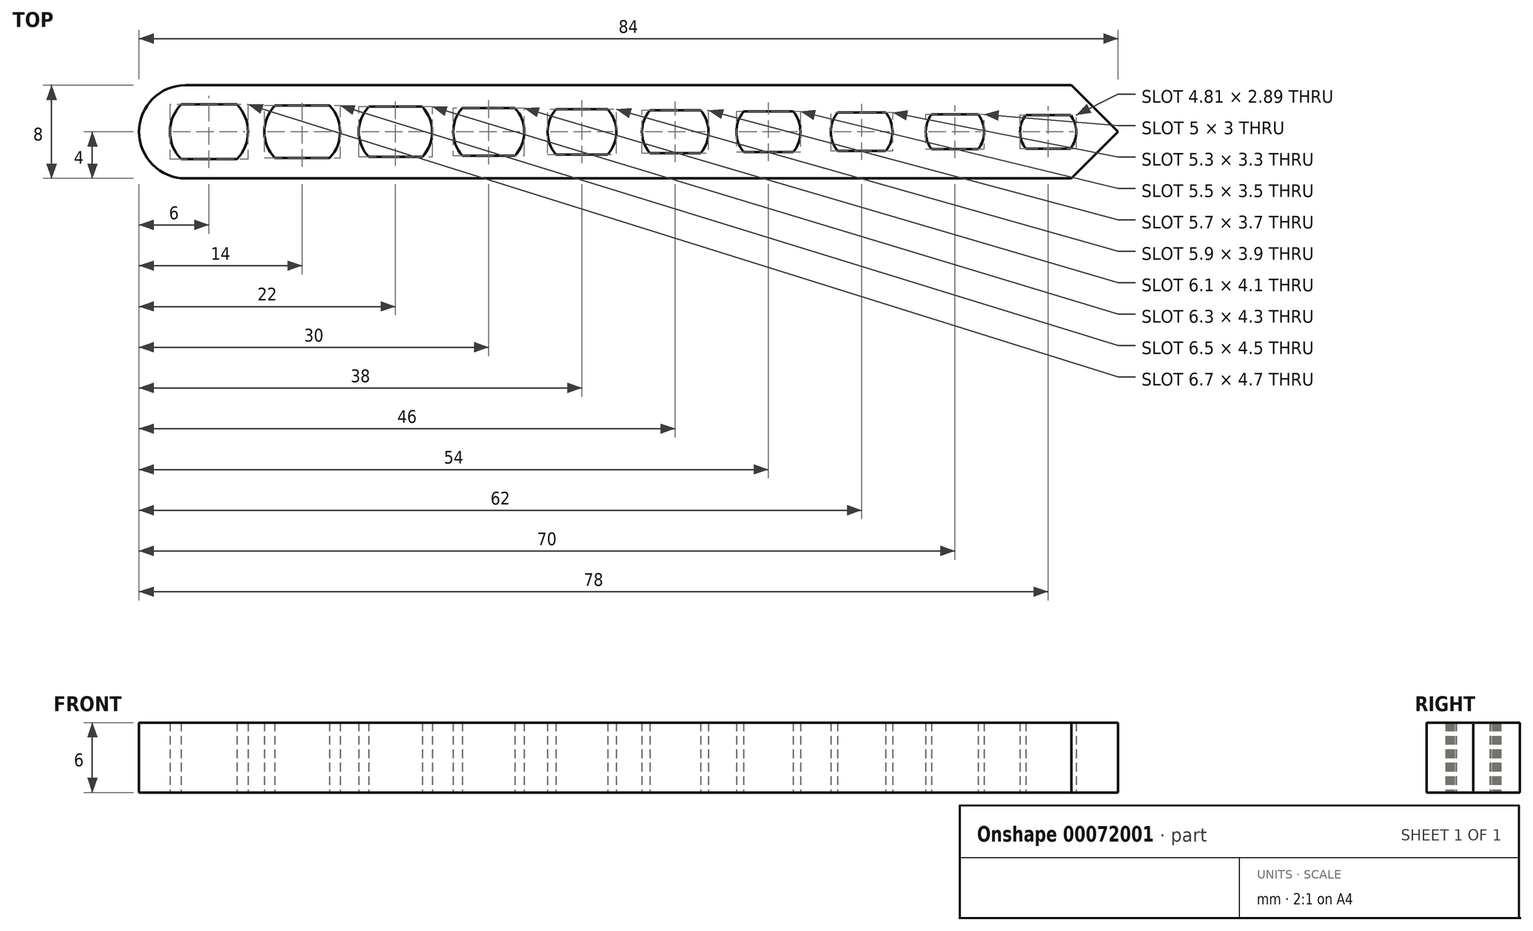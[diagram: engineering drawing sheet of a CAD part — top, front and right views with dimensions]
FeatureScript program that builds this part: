
annotation { "Feature Type Name" : "Feature", "Feature Type Description" : "" }
export const myFeature = defineFeature(function(context is Context, id is Id, definition is map)
    precondition{}
    {
        {
            var Q0;
            Q0=qCreatedBy(makeId("Top.planeOp"),FACE);
            var sketch = newSketch(context, id + "F0", { "sketchPlane" : qUnion([Q0])});
            skLineSegment(sketch, "E0.bottom", {"start": v(-38, 4) * mm, "end": v(38, 4) * mm});
            skLineSegment(sketch, "E0.top", {"start": v(-38, -4) * mm, "end": v(38, -4) * mm});
            skLineSegment(sketch, "E0.left", {"start": v(-38, 4) * mm, "end": v(-38, -4) * mm, "construction": true});
            skLineSegment(sketch, "E0.right", {"start": v(38, 4) * mm, "end": v(38, -4) * mm, "construction": true});
            skLineSegment(sketch, "E1", {"start": v(-38, 0) * mm, "end": v(38, 0) * mm, "construction": true});
            skPoint(sketch, "E1.endSnap0", {"position": v(38, 0) * mm});
            skPoint(sketch, "E2", {"position": v(0, 0) * mm});
            skArc(sketch, "E3", {"start": v(-38, -4) * mm, "mid": v(-42, 0) * mm, "end": v(-38, 4) * mm});
            skArc(sketch, "E4", {"start": v(38, -4) * mm, "mid": v(42, 0) * mm, "end": v(38, 4) * mm});
            skCircle(sketch, "E5", {"center": v(-36, 0) * mm, "radius": 3.35 * mm});
            skLineSegment(sketch, "E6", {"start": v(-38.39, 2.35) * mm, "end": v(-33.61, 2.35) * mm});
            skLineSegment(sketch, "E7", {"start": v(-38.39, -2.35) * mm, "end": v(-33.61, -2.35) * mm});
            skCircle(sketch, "E8", {"center": v(-28, 0) * mm, "radius": 3.25 * mm});
            skLineSegment(sketch, "E9", {"start": v(-30.35, 2.25) * mm, "end": v(-25.65, 2.25) * mm});
            skLineSegment(sketch, "E10", {"start": v(-30.35, -2.25) * mm, "end": v(-25.65, -2.25) * mm});
            skCircle(sketch, "E11", {"center": v(-20, 0) * mm, "radius": 3.15 * mm});
            skLineSegment(sketch, "E12", {"start": v(-22.3, 2.15) * mm, "end": v(-17.7, 2.15) * mm});
            skLineSegment(sketch, "E13", {"start": v(-22.3, -2.15) * mm, "end": v(-17.7, -2.15) * mm});
            skCircle(sketch, "E14", {"center": v(-12, 0) * mm, "radius": 3.05 * mm});
            skLineSegment(sketch, "E15", {"start": v(-14.26, 2.05) * mm, "end": v(-9.74, 2.05) * mm});
            skLineSegment(sketch, "E16", {"start": v(-14.26, -2.05) * mm, "end": v(-9.74, -2.05) * mm});
            skCircle(sketch, "E17", {"center": v(-4, 0) * mm, "radius": 2.95 * mm});
            skLineSegment(sketch, "E18", {"start": v(-6.21, 1.95) * mm, "end": v(-1.79, 1.95) * mm});
            skLineSegment(sketch, "E19", {"start": v(-6.21, -1.95) * mm, "end": v(-1.79, -1.95) * mm});
            skCircle(sketch, "E20", {"center": v(4, 0) * mm, "radius": 2.85 * mm});
            skLineSegment(sketch, "E21", {"start": v(1.83, 1.85) * mm, "end": v(6.17, 1.85) * mm});
            skLineSegment(sketch, "E22", {"start": v(1.83, -1.85) * mm, "end": v(6.17, -1.85) * mm});
            skCircle(sketch, "E23", {"center": v(12, 0) * mm, "radius": 2.75 * mm});
            skLineSegment(sketch, "E24", {"start": v(9.88, 1.75) * mm, "end": v(14.12, 1.75) * mm});
            skLineSegment(sketch, "E25", {"start": v(9.88, -1.75) * mm, "end": v(14.12, -1.75) * mm});
            skCircle(sketch, "E26", {"center": v(20, 0) * mm, "radius": 2.65 * mm});
            skLineSegment(sketch, "E27", {"start": v(17.93, 1.65) * mm, "end": v(22.07, 1.65) * mm});
            skLineSegment(sketch, "E28", {"start": v(17.93, -1.65) * mm, "end": v(22.07, -1.65) * mm});
            skCircle(sketch, "E29", {"center": v(28, 0) * mm, "radius": 2.5 * mm});
            skLineSegment(sketch, "E30", {"start": v(26, 1.5) * mm, "end": v(30, 1.5) * mm});
            skLineSegment(sketch, "E31", {"start": v(26, -1.5) * mm, "end": v(30, -1.5) * mm});
            skCircle(sketch, "E32", {"center": v(36, 0) * mm, "radius": 2.4 * mm});
            skLineSegment(sketch, "E33", {"start": v(34.08, 1.45) * mm, "end": v(37.92, 1.45) * mm});
            skLineSegment(sketch, "E34", {"start": v(34.08, -1.45) * mm, "end": v(37.92, -1.45) * mm});
            skLineSegment(sketch, "E35", {"start": v(38, 4) * mm, "end": v(42, 0) * mm});
            skLineSegment(sketch, "E36", {"start": v(42, 0) * mm, "end": v(38, -4) * mm});
            skSolve(sketch);
        }
        {
            var Q0;
            Q0=makeQuery(id+"F0.imprint","IMPRINT",FACE,{"disambiguationData":[TD([[makeQuery(id+"F0.imprint","IMPRINT",EDGE,{"derivedFrom":sQuery(id+"F0.wireOp",EDGE,"E0.bottom")}),-1.0]])]});
            var Q1;
            {var subQ0=sQuery(id+"F0.wireOp",EDGE,"E6");Q1=makeQuery(id+"F0.imprint","IMPRINT",FACE,{"disambiguationData":[TD([[makeQuery(id+"F0.imprint","IMPRINT",EDGE,{"derivedFrom":subQ0}),1.0]])]});}
            var Q2;
            {var subQ0=sQuery(id+"F0.wireOp",EDGE,"E7");Q2=makeQuery(id+"F0.imprint","IMPRINT",FACE,{"disambiguationData":[TD([[makeQuery(id+"F0.imprint","IMPRINT",EDGE,{"derivedFrom":subQ0}),-1.0]])]});}
            var Q3;
            {var subQ0=sQuery(id+"F0.wireOp",EDGE,"E9");Q3=makeQuery(id+"F0.imprint","IMPRINT",FACE,{"disambiguationData":[TD([[makeQuery(id+"F0.imprint","IMPRINT",EDGE,{"derivedFrom":subQ0}),1.0]])]});}
            var Q4;
            {var subQ0=sQuery(id+"F0.wireOp",EDGE,"E10");Q4=makeQuery(id+"F0.imprint","IMPRINT",FACE,{"disambiguationData":[TD([[makeQuery(id+"F0.imprint","IMPRINT",EDGE,{"derivedFrom":subQ0}),-1.0]])]});}
            var Q5;
            {var subQ0=sQuery(id+"F0.wireOp",EDGE,"E12");Q5=makeQuery(id+"F0.imprint","IMPRINT",FACE,{"disambiguationData":[TD([[makeQuery(id+"F0.imprint","IMPRINT",EDGE,{"derivedFrom":subQ0}),1.0]])]});}
            var Q6;
            {var subQ0=sQuery(id+"F0.wireOp",EDGE,"E13");Q6=makeQuery(id+"F0.imprint","IMPRINT",FACE,{"disambiguationData":[TD([[makeQuery(id+"F0.imprint","IMPRINT",EDGE,{"derivedFrom":subQ0}),-1.0]])]});}
            var Q7;
            {var subQ0=sQuery(id+"F0.wireOp",EDGE,"E15");Q7=makeQuery(id+"F0.imprint","IMPRINT",FACE,{"disambiguationData":[TD([[makeQuery(id+"F0.imprint","IMPRINT",EDGE,{"derivedFrom":subQ0}),1.0]])]});}
            var Q8;
            {var subQ0=sQuery(id+"F0.wireOp",EDGE,"E16");Q8=makeQuery(id+"F0.imprint","IMPRINT",FACE,{"disambiguationData":[TD([[makeQuery(id+"F0.imprint","IMPRINT",EDGE,{"derivedFrom":subQ0}),-1.0]])]});}
            var Q9;
            {var subQ0=sQuery(id+"F0.wireOp",EDGE,"E18");Q9=makeQuery(id+"F0.imprint","IMPRINT",FACE,{"disambiguationData":[TD([[makeQuery(id+"F0.imprint","IMPRINT",EDGE,{"derivedFrom":subQ0}),1.0]])]});}
            var Q10;
            {var subQ0=sQuery(id+"F0.wireOp",EDGE,"E19");Q10=makeQuery(id+"F0.imprint","IMPRINT",FACE,{"disambiguationData":[TD([[makeQuery(id+"F0.imprint","IMPRINT",EDGE,{"derivedFrom":subQ0}),-1.0]])]});}
            var Q11;
            {var subQ0=sQuery(id+"F0.wireOp",EDGE,"E21");Q11=makeQuery(id+"F0.imprint","IMPRINT",FACE,{"disambiguationData":[TD([[makeQuery(id+"F0.imprint","IMPRINT",EDGE,{"derivedFrom":subQ0}),1.0]])]});}
            var Q12;
            {var subQ0=sQuery(id+"F0.wireOp",EDGE,"E22");Q12=makeQuery(id+"F0.imprint","IMPRINT",FACE,{"disambiguationData":[TD([[makeQuery(id+"F0.imprint","IMPRINT",EDGE,{"derivedFrom":subQ0}),-1.0]])]});}
            var Q13;
            {var subQ0=sQuery(id+"F0.wireOp",EDGE,"E24");Q13=makeQuery(id+"F0.imprint","IMPRINT",FACE,{"disambiguationData":[TD([[makeQuery(id+"F0.imprint","IMPRINT",EDGE,{"derivedFrom":subQ0}),1.0]])]});}
            var Q14;
            {var subQ0=sQuery(id+"F0.wireOp",EDGE,"E25");Q14=makeQuery(id+"F0.imprint","IMPRINT",FACE,{"disambiguationData":[TD([[makeQuery(id+"F0.imprint","IMPRINT",EDGE,{"derivedFrom":subQ0}),-1.0]])]});}
            var Q15;
            {var subQ0=sQuery(id+"F0.wireOp",EDGE,"E27");Q15=makeQuery(id+"F0.imprint","IMPRINT",FACE,{"disambiguationData":[TD([[makeQuery(id+"F0.imprint","IMPRINT",EDGE,{"derivedFrom":subQ0}),1.0]])]});}
            var Q16;
            {var subQ0=sQuery(id+"F0.wireOp",EDGE,"E28");Q16=makeQuery(id+"F0.imprint","IMPRINT",FACE,{"disambiguationData":[TD([[makeQuery(id+"F0.imprint","IMPRINT",EDGE,{"derivedFrom":subQ0}),-1.0]])]});}
            var Q17;
            {var subQ0=sQuery(id+"F0.wireOp",EDGE,"E30");Q17=makeQuery(id+"F0.imprint","IMPRINT",FACE,{"disambiguationData":[TD([[makeQuery(id+"F0.imprint","IMPRINT",EDGE,{"derivedFrom":subQ0}),1.0]])]});}
            var Q18;
            {var subQ0=sQuery(id+"F0.wireOp",EDGE,"E31");Q18=makeQuery(id+"F0.imprint","IMPRINT",FACE,{"disambiguationData":[TD([[makeQuery(id+"F0.imprint","IMPRINT",EDGE,{"derivedFrom":subQ0}),-1.0]])]});}
            var Q19;
            {var subQ0=sQuery(id+"F0.wireOp",EDGE,"E33");Q19=makeQuery(id+"F0.imprint","IMPRINT",FACE,{"disambiguationData":[TD([[makeQuery(id+"F0.imprint","IMPRINT",EDGE,{"derivedFrom":subQ0}),1.0]])]});}
            var Q20;
            {var subQ0=sQuery(id+"F0.wireOp",EDGE,"E34");Q20=makeQuery(id+"F0.imprint","IMPRINT",FACE,{"disambiguationData":[TD([[makeQuery(id+"F0.imprint","IMPRINT",EDGE,{"derivedFrom":subQ0}),-1.0]])]});}
            extrude(context, id + "F1", {"entities" : qUnion([Q0, Q1, Q2, Q3, Q4, Q5, Q6, Q7, Q8, Q9, Q10, Q11, Q12, Q13, Q14, Q15, Q16, Q17, Q18, Q19, Q20]), "depth" : 6 * mm});
        }
    });
